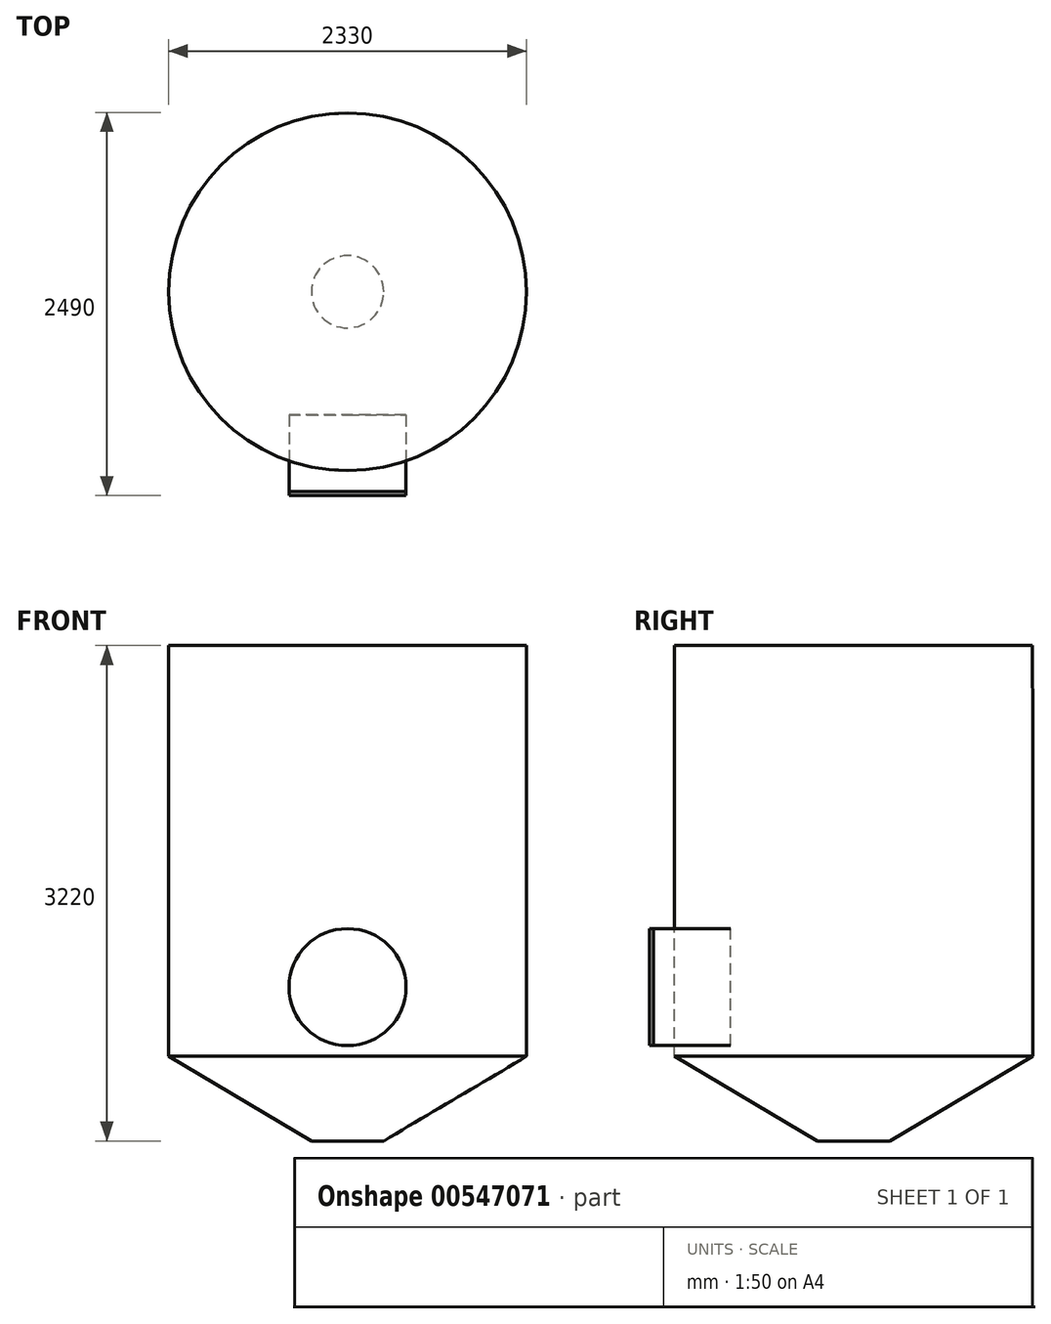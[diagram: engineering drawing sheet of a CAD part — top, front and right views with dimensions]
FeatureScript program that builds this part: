
annotation { "Feature Type Name" : "Feature", "Feature Type Description" : "" }
export const myFeature = defineFeature(function(context is Context, id is Id, definition is map)
    precondition{}
    {
        {
            var Q0;
            Q0=qCreatedBy(makeId("Front.planeOp"),FACE);
            var sketch = newSketch(context, id + "F0", { "sketchPlane" : qUnion([Q0])});
            skLineSegment(sketch, "E0", {"start": v(0, 0) * mm, "end": v(235, 0) * mm});
            skLineSegment(sketch, "E1", {"start": v(235, 0) * mm, "end": v(1165, 550) * mm});
            skLineSegment(sketch, "E2", {"start": v(1165, 550) * mm, "end": v(1165, 2662.51) * mm});
            skLineSegment(sketch, "E3", {"start": v(1165, 2662.51) * mm, "end": v(1163.1, 3220) * mm});
            skLineSegment(sketch, "E4", {"start": v(1163.1, 3220) * mm, "end": v(0, 3220) * mm});
            skLineSegment(sketch, "E5", {"start": v(0, 3220) * mm, "end": v(0, 0) * mm});
            skSolve(sketch);
        }
        {
            var Q0;
            Q0=makeQuery(id+"F0.imprint","IMPRINT",FACE,{"disambiguationData":[TD([[makeQuery(id+"F0.imprint","IMPRINT",EDGE,{"derivedFrom":sQuery(id+"F0.wireOp",EDGE,"E0")}),1.0]])]});
            var Q1;
            Q1=sQuery(id+"F0.wireOp",EDGE,"E5");
            revolve(context, id + "F1", {"entities" : qUnion([Q0]), "axis" : qUnion([Q1]), "revolveType" : RevolveType.FULL});
        }
        {
            var Q0;
            Q0=qCreatedBy(makeId("Front.planeOp"),FACE);
            cPlane(context, id + "F2", {"entities" : qUnion([Q0]), "cplaneType" : CPlaneType.OFFSET, "offset" : 1300 * mm, "width" : 150 * mm, "height" : 150 * mm});
        }
        {
            var Q0;
            Q0=qCreatedBy(id+"F2.planeOp",FACE);
            var sketch = newSketch(context, id + "F3", { "sketchPlane" : qUnion([Q0])});
            skCircle(sketch, "E6", {"center": v(0, 1000) * mm, "radius": 380 * mm});
            skSolve(sketch);
        }
        {
            var Q0;
            Q0=makeQuery(id+"F3.imprint","IMPRINT",FACE,{"disambiguationData":[TD([[makeQuery(id+"F3.imprint","IMPRINT",EDGE,{"derivedFrom":sQuery(id+"F3.wireOp",EDGE,"E6")}),1.0]])]});
            extrude(context, id + "F4", {"entities" : qUnion([Q0]), "depth" : 25 * mm, "offsetDistance" : 25 * mm});
        }
        {
            var Q0;
            Q0=makeQuery(id+"F3.imprint","IMPRINT",FACE,{"disambiguationData":[TD([[makeQuery(id+"F3.imprint","IMPRINT",EDGE,{"derivedFrom":sQuery(id+"F3.wireOp",EDGE,"E6")}),1.0]])]});
            extrude(context, id + "F5", {"entities" : qUnion([Q0]), "oppositeDirection" : true, "depth" : 500 * mm, "offsetDistance" : 25 * mm});
        }
    });
